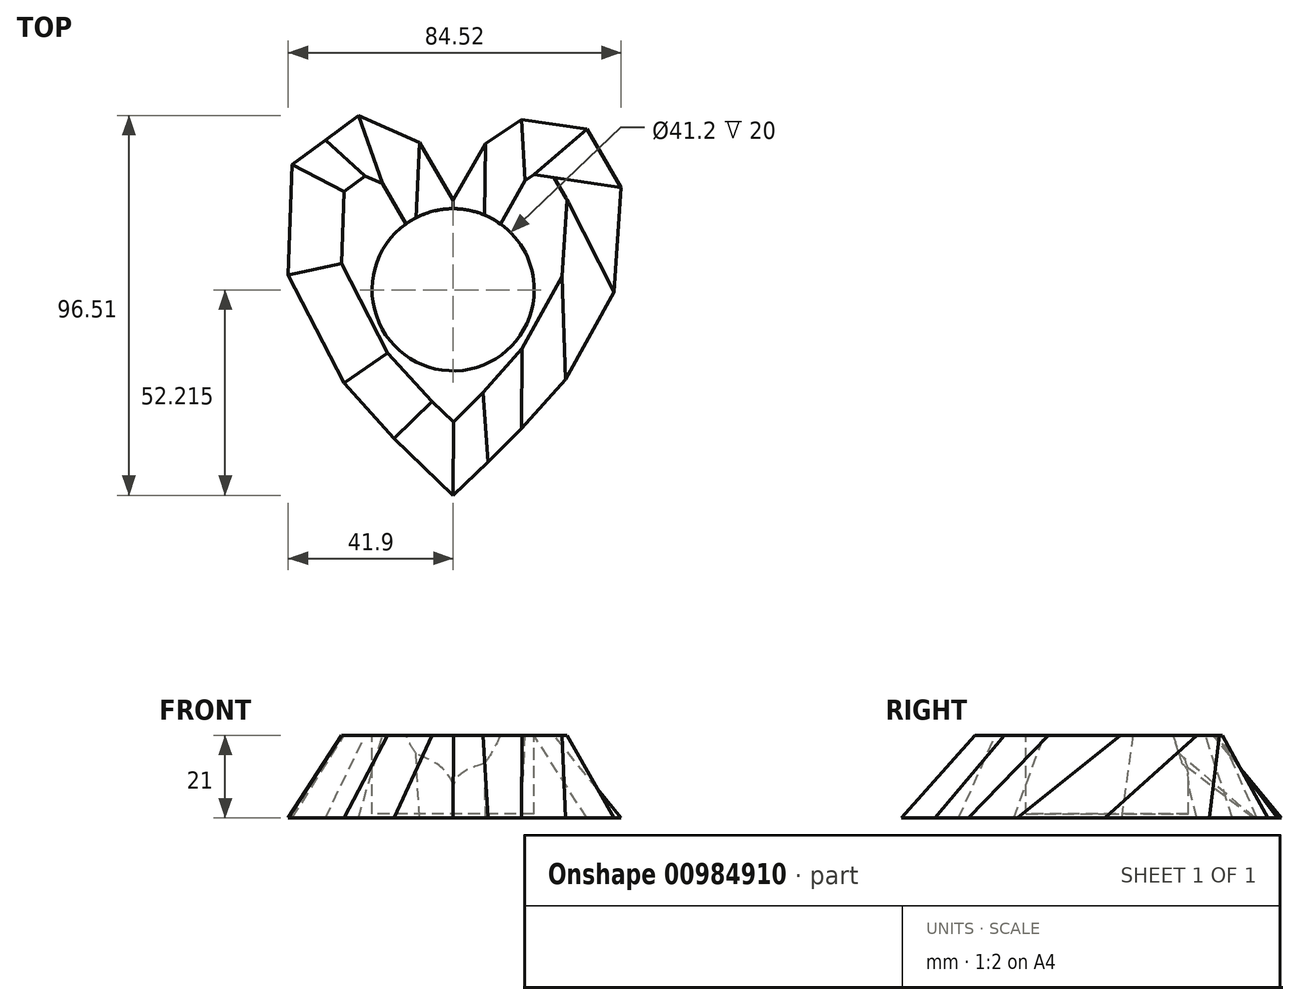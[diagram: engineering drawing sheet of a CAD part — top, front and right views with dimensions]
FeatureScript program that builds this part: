
annotation { "Feature Type Name" : "Feature", "Feature Type Description" : "" }
export const myFeature = defineFeature(function(context is Context, id is Id, definition is map)
    precondition{}
    {
        {
            var Q0;
            Q0=qCreatedBy(makeId("Top.planeOp"),FACE);
            var sketch = newSketch(context, id + "F0", { "sketchPlane" : qUnion([Q0])});
            skFitSpline(sketch, "E0", {"points": [v(0, 75) * mm, v(-35.53, 91.84) * mm, v(-42.39, 58.43) * mm, v(0, 0) * mm], "startDerivative": vector(-88.96, 244.43) * mm, "endDerivative": vector(221.24, -206.22) * mm, "construction": true});
            skLineSegment(sketch, "E1", {"start": v(0, 75) * mm, "end": v(-9.02, 99.8) * mm, "construction": true});
            skLineSegment(sketch, "E2", {"start": v(0, 0) * mm, "end": v(0, 75) * mm, "construction": true});
            skFitSpline(sketch, "E3.MirrorCS", {"points": [v(0, 75) * mm, v(35.53, 91.84) * mm, v(42.39, 58.43) * mm, v(0, 0) * mm], "startDerivative": vector(88.96, 244.43) * mm, "endDerivative": vector(-221.24, -206.22) * mm, "construction": true});
            skSolve(sketch);
        }
        {
            var Q0;
            Q0=qCreatedBy(makeId("Top.planeOp"),FACE);
            var sketch = newSketch(context, id + "F1", { "sketchPlane" : qUnion([Q0])});
            skFitSpline(sketch, "E4.0", {"points": [v(0, 75) * mm, v(9.02, 99.8) * mm, v(43.06, 99.67) * mm, v(45.48, 49.8) * mm, v(30.4, 28.34) * mm, v(0, 0) * mm], "construction": true});
            skFitSpline(sketch, "E5.0", {"points": [v(0, 75) * mm, v(-9.02, 99.8) * mm, v(-43.06, 99.67) * mm, v(-45.48, 49.8) * mm, v(-30.4, 28.34) * mm, v(0, 0) * mm], "construction": true});
            skLineSegment(sketch, "E6", {"start": v(0, 0) * mm, "end": v(-15, 14.48) * mm});
            skLineSegment(sketch, "E7", {"start": v(-15, 14.48) * mm, "end": v(-27.74, 28.5) * mm});
            skLineSegment(sketch, "E8", {"start": v(-27.74, 28.5) * mm, "end": v(-41.9, 55.9) * mm});
            skLineSegment(sketch, "E9", {"start": v(-41.9, 55.9) * mm, "end": v(-40.88, 84.06) * mm});
            skLineSegment(sketch, "E10", {"start": v(-40.88, 84.06) * mm, "end": v(-24.08, 96.5) * mm});
            skLineSegment(sketch, "E11", {"start": v(-24.08, 96.5) * mm, "end": v(-8.55, 89.68) * mm});
            skLineSegment(sketch, "E12", {"start": v(0, 75) * mm, "end": v(-8.55, 89.68) * mm});
            skLineSegment(sketch, "E13", {"start": v(0, 75) * mm, "end": v(8.22, 89.32) * mm});
            skLineSegment(sketch, "E14", {"start": v(8.22, 89.32) * mm, "end": v(17.31, 95.5) * mm});
            skLineSegment(sketch, "E15", {"start": v(17.31, 95.5) * mm, "end": v(33.97, 93.09) * mm});
            skLineSegment(sketch, "E16", {"start": v(33.97, 93.09) * mm, "end": v(42.62, 78.15) * mm});
            skLineSegment(sketch, "E17", {"start": v(42.62, 78.15) * mm, "end": v(40.81, 51.65) * mm});
            skLineSegment(sketch, "E18", {"start": v(40.81, 51.65) * mm, "end": v(28.51, 29.46) * mm});
            skLineSegment(sketch, "E19", {"start": v(28.51, 29.46) * mm, "end": v(17.37, 16.92) * mm});
            skLineSegment(sketch, "E20", {"start": v(17.37, 16.92) * mm, "end": v(8.9, 8.44) * mm});
            skLineSegment(sketch, "E21", {"start": v(8.9, 8.44) * mm, "end": v(0, 0) * mm});
            skPoint(sketch, "E22", {"position": v(-4.28, 82.34) * mm});
            skPoint(sketch, "E23", {"position": v(4.11, 83.77) * mm});
            skPoint(sketch, "E23.positionSnap0", {"position": v(4.11, 82.16) * mm});
            skSolve(sketch);
        }
        {
            assignVariable(context, id + "F2", {"variableType" : VariableType.LENGTH, "name" : "Hbougie", "lengthValue" : 20 * mm});
        }
        {
            var Q0;
            Q0=qCreatedBy(makeId("Top.planeOp"),FACE);
            cPlane(context, id + "F3", {"entities" : qUnion([Q0]), "cplaneType" : CPlaneType.OFFSET, "offset" : getVariable(context, 'Hbougie') + 1 * mm, "width" : 150 * mm, "height" : 150 * mm});
        }
        {
            var Q0;
            Q0=qCreatedBy(id+"F3.planeOp",FACE);
            var sketch = newSketch(context, id + "F4", { "sketchPlane" : qUnion([Q0])});
            skLineSegment(sketch, "E24.0.0", {"start": v(0, 0) * mm, "end": v(8.9, 8.44) * mm, "construction": true});
            skLineSegment(sketch, "E24.0.1", {"start": v(8.9, 8.44) * mm, "end": v(17.37, 16.92) * mm, "construction": true});
            skLineSegment(sketch, "E24.0.2", {"start": v(17.37, 16.92) * mm, "end": v(28.51, 29.46) * mm, "construction": true});
            skLineSegment(sketch, "E24.0.3", {"start": v(28.51, 29.46) * mm, "end": v(40.81, 51.65) * mm, "construction": true});
            skLineSegment(sketch, "E24.0.4", {"start": v(40.81, 51.65) * mm, "end": v(42.62, 78.15) * mm, "construction": true});
            skLineSegment(sketch, "E24.0.5", {"start": v(42.62, 78.15) * mm, "end": v(33.97, 93.09) * mm, "construction": true});
            skLineSegment(sketch, "E24.0.6", {"start": v(33.97, 93.09) * mm, "end": v(17.31, 95.5) * mm, "construction": true});
            skLineSegment(sketch, "E24.0.7", {"start": v(17.31, 95.5) * mm, "end": v(8.22, 89.32) * mm, "construction": true});
            skLineSegment(sketch, "E24.0.8", {"start": v(8.22, 89.32) * mm, "end": v(0, 75) * mm, "construction": true});
            skLineSegment(sketch, "E24.0.9", {"start": v(0, 75) * mm, "end": v(-8.55, 89.68) * mm, "construction": true});
            skLineSegment(sketch, "E24.0.10", {"start": v(-8.55, 89.68) * mm, "end": v(-24.08, 96.5) * mm, "construction": true});
            skLineSegment(sketch, "E24.0.11", {"start": v(-24.08, 96.5) * mm, "end": v(-40.88, 84.06) * mm, "construction": true});
            skLineSegment(sketch, "E24.0.12", {"start": v(-40.88, 84.06) * mm, "end": v(-41.9, 55.9) * mm, "construction": true});
            skLineSegment(sketch, "E24.0.13", {"start": v(-41.9, 55.9) * mm, "end": v(-27.74, 28.5) * mm, "construction": true});
            skLineSegment(sketch, "E24.0.14", {"start": v(-27.74, 28.5) * mm, "end": v(-15, 14.48) * mm, "construction": true});
            skLineSegment(sketch, "E24.0.15", {"start": v(-15, 14.48) * mm, "end": v(0, 0) * mm, "construction": true});
            skLineSegment(sketch, "E25.0", {"start": v(-17.94, 79.16) * mm, "end": v(-22.35, 81.1) * mm});
            skLineSegment(sketch, "E25.1", {"start": v(0.09, 48.24) * mm, "end": v(-9.75, 65.11) * mm, "construction": true});
            skLineSegment(sketch, "E25.2", {"start": v(18.3, 79.98) * mm, "end": v(7.92, 61.88) * mm});
            skLineSegment(sketch, "E25.3", {"start": v(20.54, 81.5) * mm, "end": v(18.3, 79.98) * mm});
            skLineSegment(sketch, "E25.4", {"start": v(-5.37, 23.82) * mm, "end": v(0.07, 18.57) * mm});
            skLineSegment(sketch, "E25.5", {"start": v(-16.65, 36.21) * mm, "end": v(-5.37, 23.82) * mm});
            skLineSegment(sketch, "E25.6", {"start": v(-28.38, 58.93) * mm, "end": v(-16.65, 36.21) * mm});
            skLineSegment(sketch, "E25.7", {"start": v(-27.72, 77.13) * mm, "end": v(-28.38, 58.93) * mm});
            skLineSegment(sketch, "E25.8", {"start": v(0.07, 18.57) * mm, "end": v(7.62, 26.12) * mm});
            skLineSegment(sketch, "E25.9", {"start": v(7.62, 26.12) * mm, "end": v(17.51, 37.25) * mm});
            skLineSegment(sketch, "E25.10", {"start": v(17.51, 37.25) * mm, "end": v(27.64, 55.54) * mm});
            skLineSegment(sketch, "E25.11", {"start": v(27.64, 55.54) * mm, "end": v(28.97, 74.98) * mm});
            skLineSegment(sketch, "E25.12", {"start": v(-22.35, 81.1) * mm, "end": v(-27.72, 77.13) * mm});
            skLineSegment(sketch, "E25.13", {"start": v(28.97, 74.98) * mm, "end": v(25.62, 80.76) * mm});
            skLineSegment(sketch, "E25.14", {"start": v(25.62, 80.76) * mm, "end": v(20.54, 81.5) * mm});
            skLineSegment(sketch, "E26", {"start": v(-9.75, 65.11) * mm, "end": v(0, 69.52) * mm});
            skLineSegment(sketch, "E27", {"start": v(0, 69.52) * mm, "end": v(7.92, 61.88) * mm});
            skLineSegment(sketch, "E28", {"start": v(-9.75, 65.11) * mm, "end": v(-17.94, 79.16) * mm});
            skLineSegment(sketch, "E29", {"start": v(7.92, 61.88) * mm, "end": v(0.09, 48.24) * mm, "construction": true});
            skSolve(sketch);
        }
        {
            var Q0;
            Q0 = qSketchRegion(id + "F1", true);
            var Q1;
            Q1 = qSketchRegion(id + "F4", true);
            var Q2;
            Q2=sQuery(id+"F0.wireOp",VERTEX,"E0.start");
            var Q3;
            Q3=sQuery(id+"F4.wireOp",VERTEX,"E26.end");
            loft(context, id + "F5", {"sheetProfilesArray" : [{ "sheetProfileEntities" : qUnion([Q0]) }, { "sheetProfileEntities" : qUnion([Q1]) }], "matchConnections" : true, "connections" : [{ "connectionEntities" : qUnion([Q2, Q3]), "connectionEdgeQueries" : qUnion([]), "connectionEdgeParameters" : [] }]});
        }
        {
            var Q0;
            Q0=qCreatedBy(id+"F3.planeOp",FACE);
            cPlane(context, id + "F6", {"entities" : qUnion([Q0]), "cplaneType" : CPlaneType.OFFSET, "offset" : 7 * mm, "width" : 150 * mm, "height" : 150 * mm});
        }
        {
            var Q0;
            Q0=makeQuery(id+"F5.opLoft","CAP_FACE",FACE,{"disambiguationData":[OSD([makeQuery(id+"F4.imprint","IMPRINT",FACE,{"disambiguationData":[TD([[makeQuery(id+"F4.imprint","IMPRINT",EDGE,{"derivedFrom":sQuery(id+"F4.wireOp",EDGE,"E25.0")}),1.0]])]})])],"isStart":true});
            var sketch = newSketch(context, id + "F7", { "sketchPlane" : qUnion([Q0])});
            skCircle(sketch, "E30", {"center": v(0, 52.22) * mm, "radius": 20.6 * mm});
            skSolve(sketch);
        }
        {
            var Q0;
            Q0 = qSketchRegion(id + "F7", true);
            extrude(context, id + "F8", {"entities" : qUnion([Q0]), "operationType" : NewBodyOperationType.REMOVE, "oppositeDirection" : true, "depth" : getVariable(context, 'Hbougie'), "offsetDistance" : 25 * mm});
        }
    });
